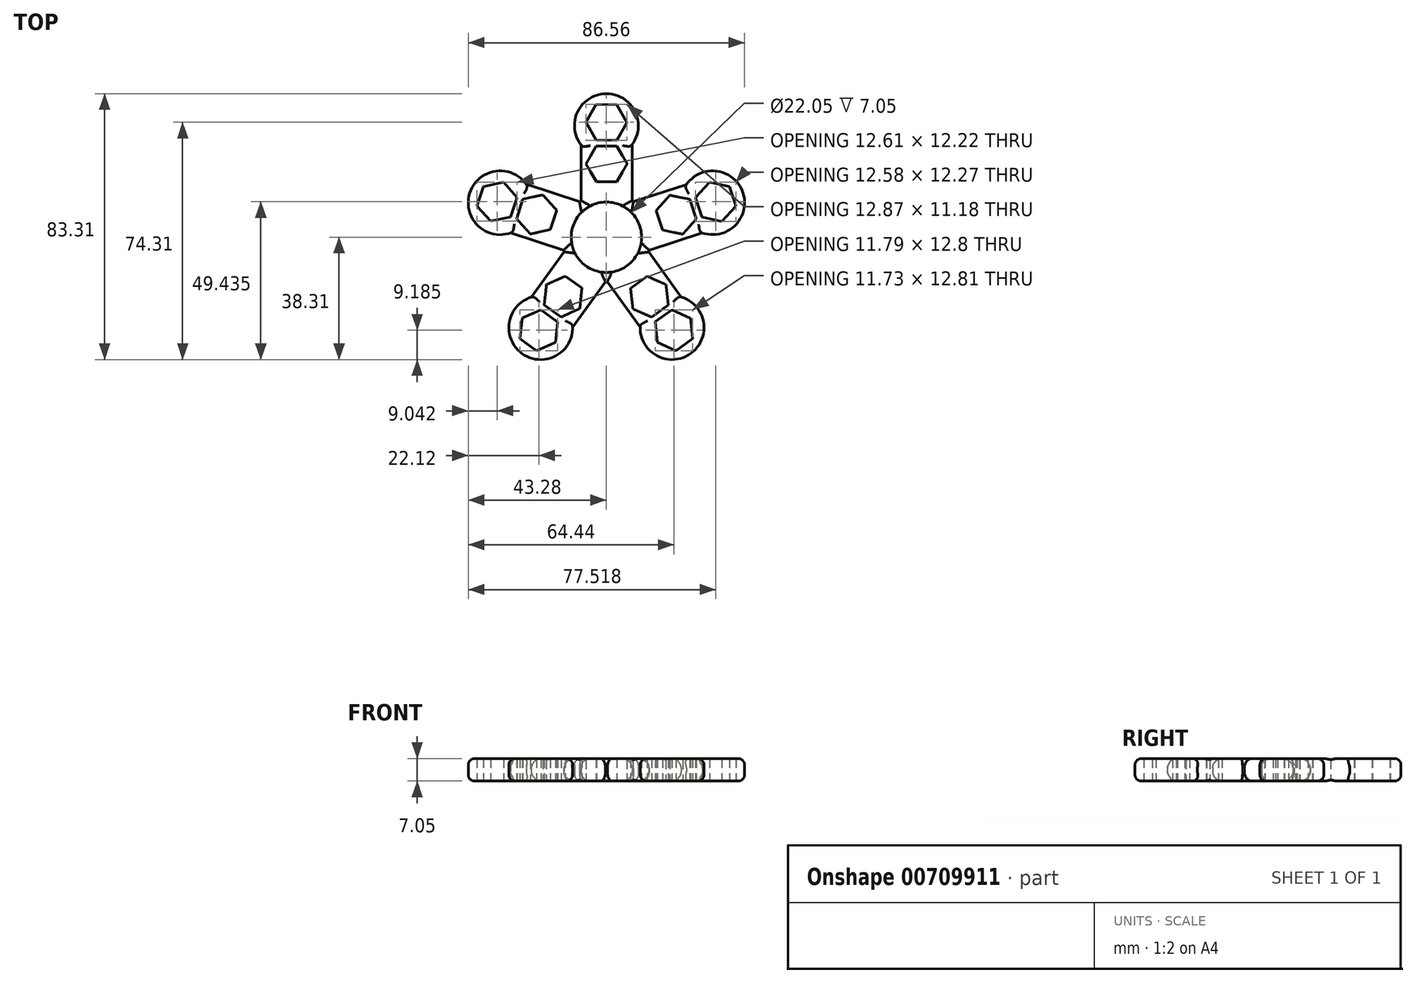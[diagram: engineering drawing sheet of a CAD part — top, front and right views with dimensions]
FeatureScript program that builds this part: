
annotation { "Feature Type Name" : "Feature", "Feature Type Description" : "" }
export const myFeature = defineFeature(function(context is Context, id is Id, definition is map)
    precondition{}
    {
        {
            var Q0;
            Q0=qCreatedBy(makeId("Top.planeOp"),FACE);
            var sketch = newSketch(context, id + "F0", { "sketchPlane" : qUnion([Q0])});
            skCircle(sketch, "E0", {"center": v(0, 0) * mm, "radius": 11.03 * mm});
            skCircle(sketch, "E1", {"center": v(0, 0) * mm, "radius": 14 * mm});
            skLineSegment(sketch, "E2.bottom", {"start": v(-7.99, 35) * mm, "end": v(8.01, 35) * mm});
            skLineSegment(sketch, "E2.top", {"start": v(-7.99, 9) * mm, "end": v(8.01, 9) * mm});
            skLineSegment(sketch, "E2.left", {"start": v(-7.99, 35) * mm, "end": v(-7.99, 9) * mm});
            skLineSegment(sketch, "E2.right", {"start": v(8.01, 35) * mm, "end": v(8.01, 9) * mm});
            skCircle(sketch, "E3", {"center": v(0, 35) * mm, "radius": 10 * mm});
            skCircle(sketch, "E4.cCircle", {"center": v(0, 36) * mm, "radius": 5.57 * mm, "construction": true});
            skLineSegment(sketch, "E4.0", {"start": v(3.2, 30.4) * mm, "end": v(-3.25, 30.44) * mm});
            skLineSegment(sketch, "E4.1", {"start": v(-3.25, 30.44) * mm, "end": v(-6.44, 36.03) * mm});
            skLineSegment(sketch, "E4.2", {"start": v(-6.44, 36.03) * mm, "end": v(-3.2, 41.6) * mm});
            skLineSegment(sketch, "E4.3", {"start": v(-3.2, 41.6) * mm, "end": v(3.25, 41.56) * mm});
            skLineSegment(sketch, "E4.4", {"start": v(3.25, 41.56) * mm, "end": v(6.44, 35.97) * mm});
            skLineSegment(sketch, "E4.5", {"start": v(6.44, 35.97) * mm, "end": v(3.2, 30.4) * mm});
            skPoint(sketch, "E4.0.midPoint", {"position": v(-0.03, 30.43) * mm});
            skCircle(sketch, "E5.cCircle", {"center": v(0.05, 23) * mm, "radius": 5.58 * mm, "construction": true});
            skLineSegment(sketch, "E5.0", {"start": v(3.3, 17.45) * mm, "end": v(-3.13, 17.4) * mm});
            skLineSegment(sketch, "E5.1", {"start": v(-3.13, 17.4) * mm, "end": v(-6.4, 22.95) * mm});
            skLineSegment(sketch, "E5.2", {"start": v(-6.4, 22.95) * mm, "end": v(-3.21, 28.55) * mm});
            skLineSegment(sketch, "E5.3", {"start": v(-3.21, 28.55) * mm, "end": v(3.22, 28.6) * mm});
            skLineSegment(sketch, "E5.4", {"start": v(3.22, 28.6) * mm, "end": v(6.48, 23.05) * mm});
            skLineSegment(sketch, "E5.5", {"start": v(6.48, 23.05) * mm, "end": v(3.3, 17.45) * mm});
            skPoint(sketch, "E5.0.midPoint", {"position": v(0.09, 17.43) * mm});
            skSolve(sketch);
        }
        {
            var Q0;
            {var subQ6=sQuery(id+"F0.wireOp",EDGE,"E4.3");Q0=makeQuery(id+"F0.imprint","IMPRINT",FACE,{"disambiguationData":[TD([[makeQuery(id+"F0.imprint","IMPRINT",EDGE,{"derivedFrom":subQ6}),1.0]])]});}
            var Q1;
            {var subQ10=sQuery(id+"F0.wireOp",EDGE,"E4.0");Q1=makeQuery(id+"F0.imprint","IMPRINT",FACE,{"disambiguationData":[TD([[makeQuery(id+"F0.imprint","IMPRINT",EDGE,{"derivedFrom":subQ10}),1.0]])]});}
            var Q2;
            Q2=makeQuery(id+"F0.imprint","IMPRINT",FACE,{"disambiguationData":[TD([[makeQuery(id+"F0.imprint","IMPRINT",EDGE,{"derivedFrom":sQuery(id+"F0.wireOp",EDGE,"E5.0")}),1.0]])]});
            var Q3;
            {var subQ1=sQuery(id+"F0.wireOp",EDGE,"E2.top");var subQ3=sQuery(id+"F0.wireOp",EDGE,"E0");var subQ4=makeQuery(id+"F0.imprint","INTERSECT",VERTEX,{"disambiguationData":[OD(0.0)],"derivedFrom":[subQ3,subQ1]});Q3=makeQuery(id+"F0.imprint","IMPRINT",FACE,{"disambiguationData":[TD([[makeQuery(id+"F0.imprint","IMPRINT",EDGE,{"disambiguationData":[TD([[subQ4,1.0]])],"derivedFrom":subQ3}),-1.0]])]});}
            var Q4;
            {var subQ1=sQuery(id+"F0.wireOp",EDGE,"E2.top");var subQ3=sQuery(id+"F0.wireOp",EDGE,"E0");var subQ7=makeQuery(id+"F0.imprint","INTERSECT",VERTEX,{"disambiguationData":[OD(0.0)],"derivedFrom":[subQ3,subQ1]});Q4=makeQuery(id+"F0.imprint","IMPRINT",FACE,{"disambiguationData":[TD([[makeQuery(id+"F0.imprint","IMPRINT",EDGE,{"disambiguationData":[TD([[subQ7,-1.0]])],"derivedFrom":subQ3}),-1.0]])]});}
            extrude(context, id + "F1", {"entities" : qUnion([Q0, Q1, Q2, Q3, Q4]), "depth" : 7.05 * mm, "offsetDistance" : 25 * mm});
        }
        {
            var Q0;
            Q0=makeQuery(id+"F1.opExtrude","SWEPT_BODY",BODY,{"disambiguationData":[OSD([sQuery(id+"F0.wireOp",EDGE,"E0"),sQuery(id+"F0.wireOp",EDGE,"E1"),sQuery(id+"F0.wireOp",EDGE,"E2.bottom"),sQuery(id+"F0.wireOp",EDGE,"E2.left"),sQuery(id+"F0.wireOp",EDGE,"E2.right"),sQuery(id+"F0.wireOp",EDGE,"E3"),sQuery(id+"F0.wireOp",EDGE,"E4.0"),sQuery(id+"F0.wireOp",EDGE,"E4.1"),sQuery(id+"F0.wireOp",EDGE,"E4.2"),sQuery(id+"F0.wireOp",EDGE,"E4.3"),sQuery(id+"F0.wireOp",EDGE,"E4.4"),sQuery(id+"F0.wireOp",EDGE,"E4.5"),sQuery(id+"F0.wireOp",EDGE,"E5.0"),sQuery(id+"F0.wireOp",EDGE,"E5.1"),sQuery(id+"F0.wireOp",EDGE,"E5.2"),sQuery(id+"F0.wireOp",EDGE,"E5.3"),sQuery(id+"F0.wireOp",EDGE,"E5.4"),sQuery(id+"F0.wireOp",EDGE,"E5.5")])]});
            var Q1;
            Q1=makeQuery(id+"F1.opExtrude","SWEPT_FACE",FACE,{"disambiguationData":[OSD([sQuery(id+"F0.wireOp",EDGE,"E1")])]});
            circularPattern(context, id + "F2", {"entities" : qUnion([Q0]), "axis" : qUnion([Q1]), "angle" : 360 * degree, "instanceCount" : 5, "equalSpace" : true});
        }
        {
            var Q0;
            Q0=makeQuery(id+"F2.opPattern","COPY",BODY,{"derivedFrom":makeQuery(id+"F1.opExtrude","SWEPT_BODY",BODY,{"disambiguationData":[OSD([sQuery(id+"F0.wireOp",EDGE,"E0"),sQuery(id+"F0.wireOp",EDGE,"E1"),sQuery(id+"F0.wireOp",EDGE,"E2.left"),sQuery(id+"F0.wireOp",EDGE,"E2.right"),sQuery(id+"F0.wireOp",EDGE,"E3"),sQuery(id+"F0.wireOp",EDGE,"E4.0"),sQuery(id+"F0.wireOp",EDGE,"E4.1"),sQuery(id+"F0.wireOp",EDGE,"E4.2"),sQuery(id+"F0.wireOp",EDGE,"E4.3"),sQuery(id+"F0.wireOp",EDGE,"E4.4"),sQuery(id+"F0.wireOp",EDGE,"E4.5"),sQuery(id+"F0.wireOp",EDGE,"E5.0"),sQuery(id+"F0.wireOp",EDGE,"E5.1"),sQuery(id+"F0.wireOp",EDGE,"E5.2"),sQuery(id+"F0.wireOp",EDGE,"E5.3"),sQuery(id+"F0.wireOp",EDGE,"E5.4"),sQuery(id+"F0.wireOp",EDGE,"E5.5")])]}),"instanceName":"2"});
            var Q1;
            Q1=makeQuery(id+"F1.opExtrude","SWEPT_BODY",BODY,{"disambiguationData":[OSD([sQuery(id+"F0.wireOp",EDGE,"E0"),sQuery(id+"F0.wireOp",EDGE,"E1"),sQuery(id+"F0.wireOp",EDGE,"E2.left"),sQuery(id+"F0.wireOp",EDGE,"E2.right"),sQuery(id+"F0.wireOp",EDGE,"E3"),sQuery(id+"F0.wireOp",EDGE,"E4.0"),sQuery(id+"F0.wireOp",EDGE,"E4.1"),sQuery(id+"F0.wireOp",EDGE,"E4.2"),sQuery(id+"F0.wireOp",EDGE,"E4.3"),sQuery(id+"F0.wireOp",EDGE,"E4.4"),sQuery(id+"F0.wireOp",EDGE,"E4.5"),sQuery(id+"F0.wireOp",EDGE,"E5.0"),sQuery(id+"F0.wireOp",EDGE,"E5.1"),sQuery(id+"F0.wireOp",EDGE,"E5.2"),sQuery(id+"F0.wireOp",EDGE,"E5.3"),sQuery(id+"F0.wireOp",EDGE,"E5.4"),sQuery(id+"F0.wireOp",EDGE,"E5.5")])]});
            var Q2;
            Q2=makeQuery(id+"F2.opPattern","COPY",BODY,{"derivedFrom":makeQuery(id+"F1.opExtrude","SWEPT_BODY",BODY,{"disambiguationData":[OSD([sQuery(id+"F0.wireOp",EDGE,"E0"),sQuery(id+"F0.wireOp",EDGE,"E1"),sQuery(id+"F0.wireOp",EDGE,"E2.left"),sQuery(id+"F0.wireOp",EDGE,"E2.right"),sQuery(id+"F0.wireOp",EDGE,"E3"),sQuery(id+"F0.wireOp",EDGE,"E4.0"),sQuery(id+"F0.wireOp",EDGE,"E4.1"),sQuery(id+"F0.wireOp",EDGE,"E4.2"),sQuery(id+"F0.wireOp",EDGE,"E4.3"),sQuery(id+"F0.wireOp",EDGE,"E4.4"),sQuery(id+"F0.wireOp",EDGE,"E4.5"),sQuery(id+"F0.wireOp",EDGE,"E5.0"),sQuery(id+"F0.wireOp",EDGE,"E5.1"),sQuery(id+"F0.wireOp",EDGE,"E5.2"),sQuery(id+"F0.wireOp",EDGE,"E5.3"),sQuery(id+"F0.wireOp",EDGE,"E5.4"),sQuery(id+"F0.wireOp",EDGE,"E5.5")])]}),"instanceName":"1"});
            var Q3;
            Q3=makeQuery(id+"F2.opPattern","COPY",BODY,{"derivedFrom":makeQuery(id+"F1.opExtrude","SWEPT_BODY",BODY,{"disambiguationData":[OSD([sQuery(id+"F0.wireOp",EDGE,"E0"),sQuery(id+"F0.wireOp",EDGE,"E1"),sQuery(id+"F0.wireOp",EDGE,"E2.left"),sQuery(id+"F0.wireOp",EDGE,"E2.right"),sQuery(id+"F0.wireOp",EDGE,"E3"),sQuery(id+"F0.wireOp",EDGE,"E4.0"),sQuery(id+"F0.wireOp",EDGE,"E4.1"),sQuery(id+"F0.wireOp",EDGE,"E4.2"),sQuery(id+"F0.wireOp",EDGE,"E4.3"),sQuery(id+"F0.wireOp",EDGE,"E4.4"),sQuery(id+"F0.wireOp",EDGE,"E4.5"),sQuery(id+"F0.wireOp",EDGE,"E5.0"),sQuery(id+"F0.wireOp",EDGE,"E5.1"),sQuery(id+"F0.wireOp",EDGE,"E5.2"),sQuery(id+"F0.wireOp",EDGE,"E5.3"),sQuery(id+"F0.wireOp",EDGE,"E5.4"),sQuery(id+"F0.wireOp",EDGE,"E5.5")])]}),"instanceName":"3"});
            var Q4;
            Q4=makeQuery(id+"F2.opPattern","COPY",BODY,{"derivedFrom":makeQuery(id+"F1.opExtrude","SWEPT_BODY",BODY,{"disambiguationData":[OSD([sQuery(id+"F0.wireOp",EDGE,"E0"),sQuery(id+"F0.wireOp",EDGE,"E1"),sQuery(id+"F0.wireOp",EDGE,"E2.left"),sQuery(id+"F0.wireOp",EDGE,"E2.right"),sQuery(id+"F0.wireOp",EDGE,"E3"),sQuery(id+"F0.wireOp",EDGE,"E4.0"),sQuery(id+"F0.wireOp",EDGE,"E4.1"),sQuery(id+"F0.wireOp",EDGE,"E4.2"),sQuery(id+"F0.wireOp",EDGE,"E4.3"),sQuery(id+"F0.wireOp",EDGE,"E4.4"),sQuery(id+"F0.wireOp",EDGE,"E4.5"),sQuery(id+"F0.wireOp",EDGE,"E5.0"),sQuery(id+"F0.wireOp",EDGE,"E5.1"),sQuery(id+"F0.wireOp",EDGE,"E5.2"),sQuery(id+"F0.wireOp",EDGE,"E5.3"),sQuery(id+"F0.wireOp",EDGE,"E5.4"),sQuery(id+"F0.wireOp",EDGE,"E5.5")])]}),"instanceName":"4"});
            booleanBodies(context, id + "F3", {"operationType" : BooleanOperationType.UNION, "tools" : qUnion([Q0, Q1, Q2, Q3, Q4])});
        }
        {
            var Q0;
            Q0=makeQuery(id+"F1.opExtrude","CAP_EDGE",EDGE,{"disambiguationData":[OSD([sQuery(id+"F0.wireOp",EDGE,"E2.left")])],"isStart":false});
            var Q1;
            Q1=makeQuery(id+"F1.opExtrude","CAP_EDGE",EDGE,{"disambiguationData":[OSD([sQuery(id+"F0.wireOp",EDGE,"E2.right")])],"isStart":true});
            var Q2;
            {var subQ0=sQuery(id+"F0.wireOp",EDGE,"E2.right");var subQ2=sQuery(id+"F0.wireOp",EDGE,"E1");Q2=makeQuery(id+"F3.opBoolean","SPLIT",EDGE,{"disambiguationData":[TD([makeQuery(id+"F1.opExtrude","SWEPT_FACE",FACE,{"disambiguationData":[OSD([subQ0])]})])],"derivedFrom":makeQuery(id+"F2.opPattern","COPY",EDGE,{"derivedFrom":makeQuery(id+"F1.opExtrude","CAP_EDGE",EDGE,{"disambiguationData":[OSD([subQ2])],"isStart":false}),"instanceName":"2"})});}
            var Q3;
            {var subQ1=sQuery(id+"F0.wireOp",EDGE,"E2.left");var subQ2=sQuery(id+"F0.wireOp",EDGE,"E1");Q3=makeQuery(id+"F3.opBoolean","SPLIT",EDGE,{"disambiguationData":[TD([makeQuery(id+"F1.opExtrude","SWEPT_FACE",FACE,{"disambiguationData":[OSD([subQ1])]})])],"derivedFrom":makeQuery(id+"F2.opPattern","COPY",EDGE,{"derivedFrom":makeQuery(id+"F1.opExtrude","CAP_EDGE",EDGE,{"disambiguationData":[OSD([subQ2])],"isStart":false}),"instanceName":"2"})});}
            var Q4;
            Q4=makeQuery(id+"F2.opPattern","COPY",EDGE,{"derivedFrom":makeQuery(id+"F1.opExtrude","CAP_EDGE",EDGE,{"disambiguationData":[OSD([sQuery(id+"F0.wireOp",EDGE,"E2.right")])],"isStart":false}),"instanceName":"2"});
            var Q5;
            Q5=makeQuery(id+"F2.opPattern","COPY",EDGE,{"derivedFrom":makeQuery(id+"F1.opExtrude","CAP_EDGE",EDGE,{"disambiguationData":[OSD([sQuery(id+"F0.wireOp",EDGE,"E2.left")])],"isStart":true}),"instanceName":"2"});
            var Q6;
            {var subQ0=sQuery(id+"F0.wireOp",EDGE,"E2.right");var subQ2=sQuery(id+"F0.wireOp",EDGE,"E1");Q6=makeQuery(id+"F3.opBoolean","SPLIT",EDGE,{"disambiguationData":[TD([makeQuery(id+"F2.opPattern","COPY",FACE,{"derivedFrom":makeQuery(id+"F1.opExtrude","SWEPT_FACE",FACE,{"disambiguationData":[OSD([subQ0])]}),"instanceName":"1"})])],"derivedFrom":makeQuery(id+"F2.opPattern","COPY",EDGE,{"derivedFrom":makeQuery(id+"F1.opExtrude","CAP_EDGE",EDGE,{"disambiguationData":[OSD([subQ2])],"isStart":true}),"instanceName":"2"})});}
            var Q7;
            Q7=makeQuery(id+"F2.opPattern","COPY",EDGE,{"derivedFrom":makeQuery(id+"F1.opExtrude","CAP_EDGE",EDGE,{"disambiguationData":[OSD([sQuery(id+"F0.wireOp",EDGE,"E2.right")])],"isStart":true}),"instanceName":"1"});
            var Q8;
            Q8=makeQuery(id+"F2.opPattern","COPY",EDGE,{"derivedFrom":makeQuery(id+"F1.opExtrude","CAP_EDGE",EDGE,{"disambiguationData":[OSD([sQuery(id+"F0.wireOp",EDGE,"E2.left")])],"isStart":false}),"instanceName":"1"});
            var Q9;
            Q9=makeQuery(id+"F2.opPattern","COPY",EDGE,{"derivedFrom":makeQuery(id+"F1.opExtrude","CAP_EDGE",EDGE,{"disambiguationData":[OSD([sQuery(id+"F0.wireOp",EDGE,"E2.left")])],"isStart":false}),"instanceName":"2"});
            var Q10;
            Q10=makeQuery(id+"F2.opPattern","COPY",EDGE,{"derivedFrom":makeQuery(id+"F1.opExtrude","CAP_EDGE",EDGE,{"disambiguationData":[OSD([sQuery(id+"F0.wireOp",EDGE,"E2.right")])],"isStart":false}),"instanceName":"1"});
            var Q11;
            {var subQ0=sQuery(id+"F0.wireOp",EDGE,"E2.right");var subQ2=sQuery(id+"F0.wireOp",EDGE,"E1");Q11=makeQuery(id+"F3.opBoolean","SPLIT",EDGE,{"disambiguationData":[TD([makeQuery(id+"F2.opPattern","COPY",FACE,{"derivedFrom":makeQuery(id+"F1.opExtrude","SWEPT_FACE",FACE,{"disambiguationData":[OSD([subQ0])]}),"instanceName":"1"})])],"derivedFrom":makeQuery(id+"F2.opPattern","COPY",EDGE,{"derivedFrom":makeQuery(id+"F1.opExtrude","CAP_EDGE",EDGE,{"disambiguationData":[OSD([subQ2])],"isStart":false}),"instanceName":"2"})});}
            var Q12;
            Q12=makeQuery(id+"F2.opPattern","COPY",EDGE,{"derivedFrom":makeQuery(id+"F1.opExtrude","CAP_EDGE",EDGE,{"disambiguationData":[OSD([sQuery(id+"F0.wireOp",EDGE,"E2.left")])],"isStart":true}),"instanceName":"1"});
            var Q13;
            {var subQ0=sQuery(id+"F0.wireOp",EDGE,"E2.right");var subQ2=sQuery(id+"F0.wireOp",EDGE,"E1");Q13=makeQuery(id+"F3.opBoolean","SPLIT",EDGE,{"disambiguationData":[TD([makeQuery(id+"F1.opExtrude","SWEPT_FACE",FACE,{"disambiguationData":[OSD([subQ0])]})])],"derivedFrom":makeQuery(id+"F2.opPattern","COPY",EDGE,{"derivedFrom":makeQuery(id+"F1.opExtrude","CAP_EDGE",EDGE,{"disambiguationData":[OSD([subQ2])],"isStart":true}),"instanceName":"2"})});}
            var Q14;
            Q14=makeQuery(id+"F1.opExtrude","CAP_EDGE",EDGE,{"disambiguationData":[OSD([sQuery(id+"F0.wireOp",EDGE,"E2.right")])],"isStart":false});
            var Q15;
            Q15=makeQuery(id+"F1.opExtrude","CAP_EDGE",EDGE,{"disambiguationData":[OSD([sQuery(id+"F0.wireOp",EDGE,"E2.left")])],"isStart":true});
            var Q16;
            {var subQ1=sQuery(id+"F0.wireOp",EDGE,"E2.left");var subQ2=sQuery(id+"F0.wireOp",EDGE,"E1");Q16=makeQuery(id+"F3.opBoolean","SPLIT",EDGE,{"disambiguationData":[TD([makeQuery(id+"F1.opExtrude","SWEPT_FACE",FACE,{"disambiguationData":[OSD([subQ1])]})])],"derivedFrom":makeQuery(id+"F2.opPattern","COPY",EDGE,{"derivedFrom":makeQuery(id+"F1.opExtrude","CAP_EDGE",EDGE,{"disambiguationData":[OSD([subQ2])],"isStart":true}),"instanceName":"2"})});}
            var Q17;
            Q17=makeQuery(id+"F2.opPattern","COPY",EDGE,{"derivedFrom":makeQuery(id+"F1.opExtrude","CAP_EDGE",EDGE,{"disambiguationData":[OSD([sQuery(id+"F0.wireOp",EDGE,"E2.right")])],"isStart":true}),"instanceName":"2"});
            var Q18;
            Q18=makeQuery(id+"F2.opPattern","COPY",EDGE,{"derivedFrom":makeQuery(id+"F1.opExtrude","CAP_EDGE",EDGE,{"disambiguationData":[OSD([sQuery(id+"F0.wireOp",EDGE,"E2.left")])],"isStart":false}),"instanceName":"3"});
            var Q19;
            Q19=makeQuery(id+"F2.opPattern","COPY",EDGE,{"derivedFrom":makeQuery(id+"F1.opExtrude","CAP_EDGE",EDGE,{"disambiguationData":[OSD([sQuery(id+"F0.wireOp",EDGE,"E2.right")])],"isStart":false}),"instanceName":"3"});
            var Q20;
            Q20=makeQuery(id+"F2.opPattern","COPY",EDGE,{"derivedFrom":makeQuery(id+"F1.opExtrude","CAP_EDGE",EDGE,{"disambiguationData":[OSD([sQuery(id+"F0.wireOp",EDGE,"E2.left")])],"isStart":false}),"instanceName":"4"});
            var Q21;
            Q21=makeQuery(id+"F2.opPattern","COPY",EDGE,{"derivedFrom":makeQuery(id+"F1.opExtrude","CAP_EDGE",EDGE,{"disambiguationData":[OSD([sQuery(id+"F0.wireOp",EDGE,"E2.right")])],"isStart":false}),"instanceName":"4"});
            var Q22;
            Q22=makeQuery(id+"F2.opPattern","COPY",EDGE,{"derivedFrom":makeQuery(id+"F1.opExtrude","CAP_EDGE",EDGE,{"disambiguationData":[OSD([sQuery(id+"F0.wireOp",EDGE,"E2.right")])],"isStart":true}),"instanceName":"4"});
            var Q23;
            Q23=makeQuery(id+"F2.opPattern","COPY",EDGE,{"derivedFrom":makeQuery(id+"F1.opExtrude","CAP_EDGE",EDGE,{"disambiguationData":[OSD([sQuery(id+"F0.wireOp",EDGE,"E2.left")])],"isStart":true}),"instanceName":"4"});
            var Q24;
            Q24=makeQuery(id+"F2.opPattern","COPY",EDGE,{"derivedFrom":makeQuery(id+"F1.opExtrude","CAP_EDGE",EDGE,{"disambiguationData":[OSD([sQuery(id+"F0.wireOp",EDGE,"E2.right")])],"isStart":true}),"instanceName":"3"});
            var Q25;
            Q25=makeQuery(id+"F2.opPattern","COPY",EDGE,{"derivedFrom":makeQuery(id+"F1.opExtrude","CAP_EDGE",EDGE,{"disambiguationData":[OSD([sQuery(id+"F0.wireOp",EDGE,"E2.left")])],"isStart":true}),"instanceName":"3"});
            var Q26;
            {var subQ0=sQuery(id+"F0.wireOp",EDGE,"E1");var subQ1=sQuery(id+"F0.wireOp",EDGE,"E2.right");Q26=makeQuery(id+"F3.opBoolean","SPLIT",EDGE,{"disambiguationData":[TD([makeQuery(id+"F2.opPattern","COPY",FACE,{"derivedFrom":makeQuery(id+"F1.opExtrude","SWEPT_FACE",FACE,{"disambiguationData":[OSD([subQ1])]}),"instanceName":"2"})])],"derivedFrom":makeQuery(id+"F2.opPattern","COPY",EDGE,{"derivedFrom":makeQuery(id+"F1.opExtrude","CAP_EDGE",EDGE,{"disambiguationData":[OSD([subQ0])],"isStart":true}),"instanceName":"2"})});}
            var Q27;
            {var subQ0=sQuery(id+"F0.wireOp",EDGE,"E1");var subQ1=sQuery(id+"F0.wireOp",EDGE,"E2.right");Q27=makeQuery(id+"F3.opBoolean","SPLIT",EDGE,{"disambiguationData":[TD([makeQuery(id+"F2.opPattern","COPY",FACE,{"derivedFrom":makeQuery(id+"F1.opExtrude","SWEPT_FACE",FACE,{"disambiguationData":[OSD([subQ1])]}),"instanceName":"3"})])],"derivedFrom":makeQuery(id+"F2.opPattern","COPY",EDGE,{"derivedFrom":makeQuery(id+"F1.opExtrude","CAP_EDGE",EDGE,{"disambiguationData":[OSD([subQ0])],"isStart":true}),"instanceName":"2"})});}
            var Q28;
            {var subQ0=sQuery(id+"F0.wireOp",EDGE,"E1");var subQ1=sQuery(id+"F0.wireOp",EDGE,"E2.right");Q28=makeQuery(id+"F3.opBoolean","SPLIT",EDGE,{"disambiguationData":[TD([makeQuery(id+"F2.opPattern","COPY",FACE,{"derivedFrom":makeQuery(id+"F1.opExtrude","SWEPT_FACE",FACE,{"disambiguationData":[OSD([subQ1])]}),"instanceName":"2"})])],"derivedFrom":makeQuery(id+"F2.opPattern","COPY",EDGE,{"derivedFrom":makeQuery(id+"F1.opExtrude","CAP_EDGE",EDGE,{"disambiguationData":[OSD([subQ0])],"isStart":false}),"instanceName":"2"})});}
            var Q29;
            {var subQ0=sQuery(id+"F0.wireOp",EDGE,"E1");var subQ1=sQuery(id+"F0.wireOp",EDGE,"E2.right");Q29=makeQuery(id+"F3.opBoolean","SPLIT",EDGE,{"disambiguationData":[TD([makeQuery(id+"F2.opPattern","COPY",FACE,{"derivedFrom":makeQuery(id+"F1.opExtrude","SWEPT_FACE",FACE,{"disambiguationData":[OSD([subQ1])]}),"instanceName":"3"})])],"derivedFrom":makeQuery(id+"F2.opPattern","COPY",EDGE,{"derivedFrom":makeQuery(id+"F1.opExtrude","CAP_EDGE",EDGE,{"disambiguationData":[OSD([subQ0])],"isStart":false}),"instanceName":"2"})});}
            fillet(context, id + "F4", {"entities" : qUnion([Q0, Q1, Q2, Q3, Q4, Q5, Q6, Q7, Q8, Q9, Q10, Q11, Q12, Q13, Q14, Q15, Q16, Q17, Q18, Q19, Q20, Q21, Q22, Q23, Q24, Q25, Q26, Q27, Q28, Q29]), "radius" : 3 * mm, "tangentPropagation" : true, "allowEdgeOverflow" : false});
        }
        {
            var Q0;
            Q0=makeQuery(id+"F1.opExtrude","CAP_EDGE",EDGE,{"disambiguationData":[OSD([sQuery(id+"F0.wireOp",EDGE,"E3")])],"isStart":false});
            var Q1;
            Q1=makeQuery(id+"F2.opPattern","COPY",EDGE,{"derivedFrom":makeQuery(id+"F1.opExtrude","CAP_EDGE",EDGE,{"disambiguationData":[OSD([sQuery(id+"F0.wireOp",EDGE,"E3")])],"isStart":false}),"instanceName":"2"});
            var Q2;
            Q2=makeQuery(id+"F2.opPattern","COPY",EDGE,{"derivedFrom":makeQuery(id+"F1.opExtrude","CAP_EDGE",EDGE,{"disambiguationData":[OSD([sQuery(id+"F0.wireOp",EDGE,"E3")])],"isStart":false}),"instanceName":"1"});
            var Q3;
            Q3=makeQuery(id+"F1.opExtrude","CAP_EDGE",EDGE,{"disambiguationData":[OSD([sQuery(id+"F0.wireOp",EDGE,"E3")])],"isStart":true});
            var Q4;
            Q4=makeQuery(id+"F2.opPattern","COPY",EDGE,{"derivedFrom":makeQuery(id+"F1.opExtrude","CAP_EDGE",EDGE,{"disambiguationData":[OSD([sQuery(id+"F0.wireOp",EDGE,"E3")])],"isStart":true}),"instanceName":"1"});
            var Q5;
            Q5=makeQuery(id+"F2.opPattern","COPY",EDGE,{"derivedFrom":makeQuery(id+"F1.opExtrude","CAP_EDGE",EDGE,{"disambiguationData":[OSD([sQuery(id+"F0.wireOp",EDGE,"E3")])],"isStart":true}),"instanceName":"2"});
            var Q6;
            Q6=makeQuery(id+"F2.opPattern","COPY",EDGE,{"derivedFrom":makeQuery(id+"F1.opExtrude","CAP_EDGE",EDGE,{"disambiguationData":[OSD([sQuery(id+"F0.wireOp",EDGE,"E3")])],"isStart":true}),"instanceName":"3"});
            var Q7;
            Q7=makeQuery(id+"F2.opPattern","COPY",EDGE,{"derivedFrom":makeQuery(id+"F1.opExtrude","CAP_EDGE",EDGE,{"disambiguationData":[OSD([sQuery(id+"F0.wireOp",EDGE,"E3")])],"isStart":false}),"instanceName":"3"});
            var Q8;
            Q8=makeQuery(id+"F2.opPattern","COPY",EDGE,{"derivedFrom":makeQuery(id+"F1.opExtrude","CAP_EDGE",EDGE,{"disambiguationData":[OSD([sQuery(id+"F0.wireOp",EDGE,"E3")])],"isStart":true}),"instanceName":"4"});
            var Q9;
            Q9=makeQuery(id+"F2.opPattern","COPY",EDGE,{"derivedFrom":makeQuery(id+"F1.opExtrude","CAP_EDGE",EDGE,{"disambiguationData":[OSD([sQuery(id+"F0.wireOp",EDGE,"E3")])],"isStart":false}),"instanceName":"4"});
            fillet(context, id + "F5", {"entities" : qUnion([Q0, Q1, Q2, Q3, Q4, Q5, Q6, Q7, Q8, Q9]), "radius" : 2 * mm, "tangentPropagation" : true, "allowEdgeOverflow" : false});
        }
    });
